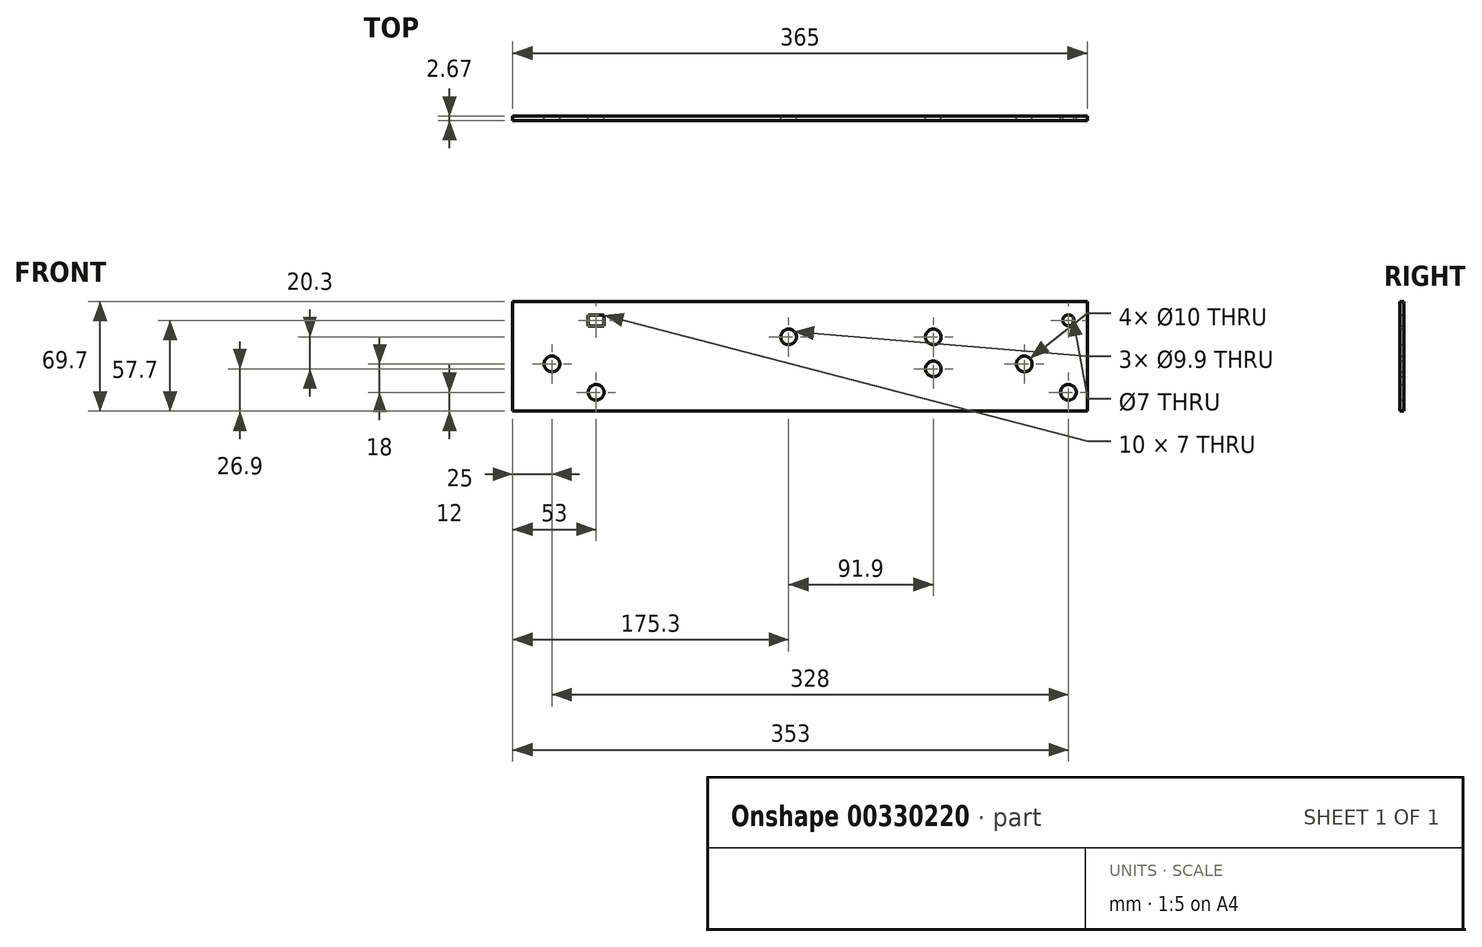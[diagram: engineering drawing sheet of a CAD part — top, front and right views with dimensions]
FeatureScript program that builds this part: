
annotation { "Feature Type Name" : "Feature", "Feature Type Description" : "" }
export const myFeature = defineFeature(function(context is Context, id is Id, definition is map)
    precondition{}
    {
        {
            var Q0;
            Q0=qCreatedBy(makeId("Front.planeOp"),FACE);
            var sketch = newSketch(context, id + "F0", { "sketchPlane" : qUnion([Q0])});
            skLineSegment(sketch, "E0.bottom", {"start": v(0, 0) * mm, "end": v(365, 0) * mm});
            skLineSegment(sketch, "E0.top", {"start": v(0, 69.7) * mm, "end": v(365, 69.7) * mm});
            skLineSegment(sketch, "E0.left", {"start": v(0, 0) * mm, "end": v(0, 69.7) * mm});
            skLineSegment(sketch, "E0.right", {"start": v(365, 0) * mm, "end": v(365, 69.7) * mm});
            skCircle(sketch, "E1", {"center": v(353, 57.7) * mm, "radius": 3.5 * mm});
            skCircle(sketch, "E2", {"center": v(353, 12) * mm, "radius": 5 * mm});
            skCircle(sketch, "E3", {"center": v(267.2, 47.2) * mm, "radius": 4.95 * mm});
            skCircle(sketch, "E4", {"center": v(325, 30) * mm, "radius": 5 * mm});
            skCircle(sketch, "E5", {"center": v(175.3, 47.2) * mm, "radius": 4.95 * mm});
            skCircle(sketch, "E6", {"center": v(25, 30) * mm, "radius": 5 * mm});
            skCircle(sketch, "E7", {"center": v(267.2, 26.9) * mm, "radius": 4.95 * mm});
            skCircle(sketch, "E8", {"center": v(53, 12) * mm, "radius": 5 * mm});
            skLineSegment(sketch, "E9.bottom", {"start": v(48, 61.2) * mm, "end": v(58, 61.2) * mm});
            skLineSegment(sketch, "E9.top", {"start": v(48, 54.2) * mm, "end": v(58, 54.2) * mm});
            skLineSegment(sketch, "E9.left", {"start": v(48, 61.2) * mm, "end": v(48, 54.2) * mm});
            skLineSegment(sketch, "E9.right", {"start": v(58, 61.2) * mm, "end": v(58, 54.2) * mm});
            skSolve(sketch);
        }
        {
            var Q0;
            Q0 = qSketchRegion(id + "F0", true);
            var Q1;
            Q1=makeQuery(id+"F0.imprint","IMPRINT",FACE,{"disambiguationData":[TD([[makeQuery(id+"F0.imprint","IMPRINT",EDGE,{"derivedFrom":sQuery(id+"F0.wireOp",EDGE,"E0.bottom")}),1.0]])]});
            extrude(context, id + "F1", {"entities" : qUnion([Q0, Q1]), "depth" : 2.67 * mm});
        }
    });
